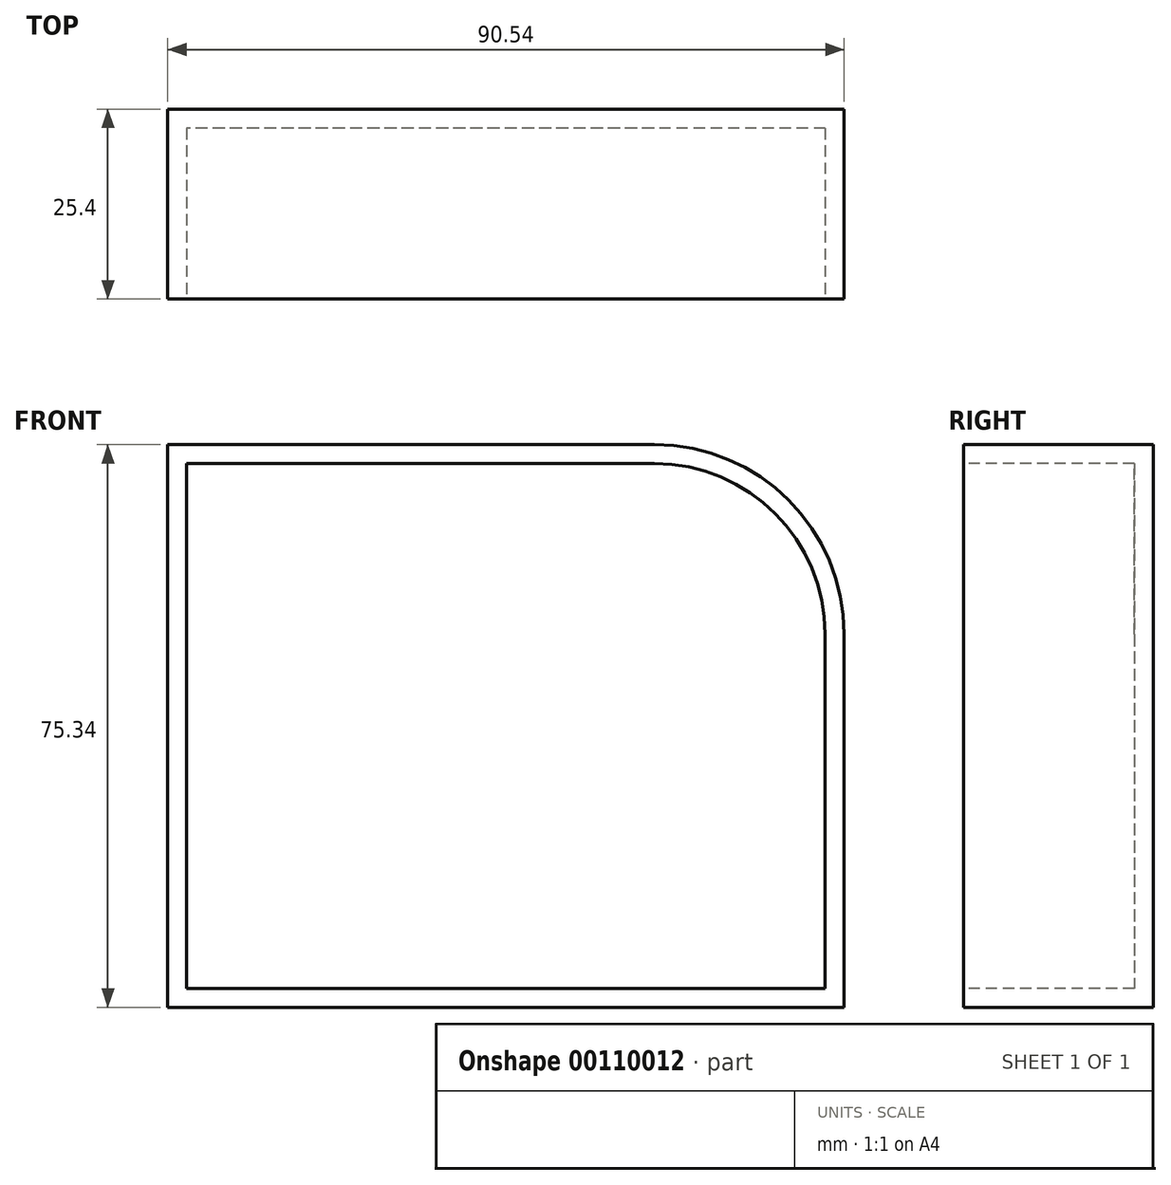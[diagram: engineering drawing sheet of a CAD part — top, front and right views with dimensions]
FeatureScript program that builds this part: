
annotation { "Feature Type Name" : "Feature", "Feature Type Description" : "" }
export const myFeature = defineFeature(function(context is Context, id is Id, definition is map)
    precondition{}
    {
        {
            var Q0;
            Q0=qCreatedBy(makeId("Front.planeOp"),FACE);
            var sketch = newSketch(context, id + "F0", { "sketchPlane" : qUnion([Q0])});
            skLineSegment(sketch, "E0.bottom", {"start": v(45.27, 37.67) * mm, "end": v(-45.27, 37.67) * mm});
            skLineSegment(sketch, "E0.top", {"start": v(45.27, -37.67) * mm, "end": v(-45.27, -37.67) * mm});
            skLineSegment(sketch, "E0.left", {"start": v(45.27, 37.67) * mm, "end": v(45.27, -37.67) * mm});
            skLineSegment(sketch, "E0.right", {"start": v(-45.27, 37.67) * mm, "end": v(-45.27, -37.67) * mm});
            skPoint(sketch, "E0.middle", {"position": v(0, 0) * mm});
            skSolve(sketch);
        }
        {
            var Q0;
            Q0=makeQuery(id+"F0.imprint","IMPRINT",FACE,{"disambiguationData":[TD([[makeQuery(id+"F0.imprint","IMPRINT",EDGE,{"derivedFrom":sQuery(id+"F0.wireOp",EDGE,"E0.bottom")}),1.0]])]});
            extrude(context, id + "F1", {"entities" : qUnion([Q0]), "oppositeDirection" : true, "depth" : 25.4 * mm});
        }
        {
            var Q0;
            Q0=makeQuery(id+"F1.opExtrude","SWEPT_EDGE",EDGE,{"disambiguationData":[OSD([sQuery(id+"F0.wireOp",EDGE,"E0.bottom"),sQuery(id+"F0.wireOp",EDGE,"E0.left")])]});
            fillet(context, id + "F2", {"entities" : qUnion([Q0]), "radius" : 25.4 * mm, "tangentPropagation" : true, "allowEdgeOverflow" : false});
        }
        {
            var Q0;
            Q0=makeQuery(id+"F1.opExtrude","CAP_FACE",FACE,{"disambiguationData":[OSD([sQuery(id+"F0.wireOp",EDGE,"E0.bottom"),sQuery(id+"F0.wireOp",EDGE,"E0.top"),sQuery(id+"F0.wireOp",EDGE,"E0.left"),sQuery(id+"F0.wireOp",EDGE,"E0.right")])],"isStart":true});
            shell(context, id + "F3", {"entities" : qUnion([Q0]), "thickness" : 2.54 * mm});
        }
    });
